# Revit family: Shower_Arm-GROHE-Eurocube-27712000
name_source: partatom
category: Plumbing Fixtures
revit_build: Autodesk Revit 2014 (Build: 20130308_1515(x64)
units: mm (PartAtom-declared; Revit-internal decimal feet)

## types (1)
- Shower_Arm-GROHE-Eurocube-27712000
    Assembly Code = D2010710
    CW Connection = Yes
    CWFU = 3
    CalGreen Compliant = Yes
    Cold Water Connection Diameter = 1/2"
    Cold Water Connection Radius = 1/4"
    Default Elevation = 0"
    Description = Eurocube 6 In. Ceiling Shower Arm
    Finish = Metal-Grohe-000-Chrome
    Flow Rate = 2.0 gpm (7.6 L/min)
    HW Connection = Yes
    HWFU = 3
    Height = 6 1/16"
    Hot Water Connection Diameter = 1"
    Hot Water Connection Radius = 1/4"
    Installation Type = Ceiling-Mount
    Manufacturer = Grohe
    Material = Metal-Grohe-000-Chrome
    Model = 27712000
    Price = Prices may vary. Please consult Manufacturer Representative for most up-to-date price list.
    Product Page URL = https://www.grohe.us
    Tempered Connection Diameter = 1/2"
    Tempered Connection Radius = 1/4"
    URL = https://www.grohe.us
    Vent Connection = No
    WFU = 4
    Warranty Documentation Link = https://cdn.cloud.grohe.com
    Waste Connection = No
    cUPC Compliant = Yes

## geometry (parser evidence)
native form markers: Sweep x1
no freeform markers — native parametric forms only
